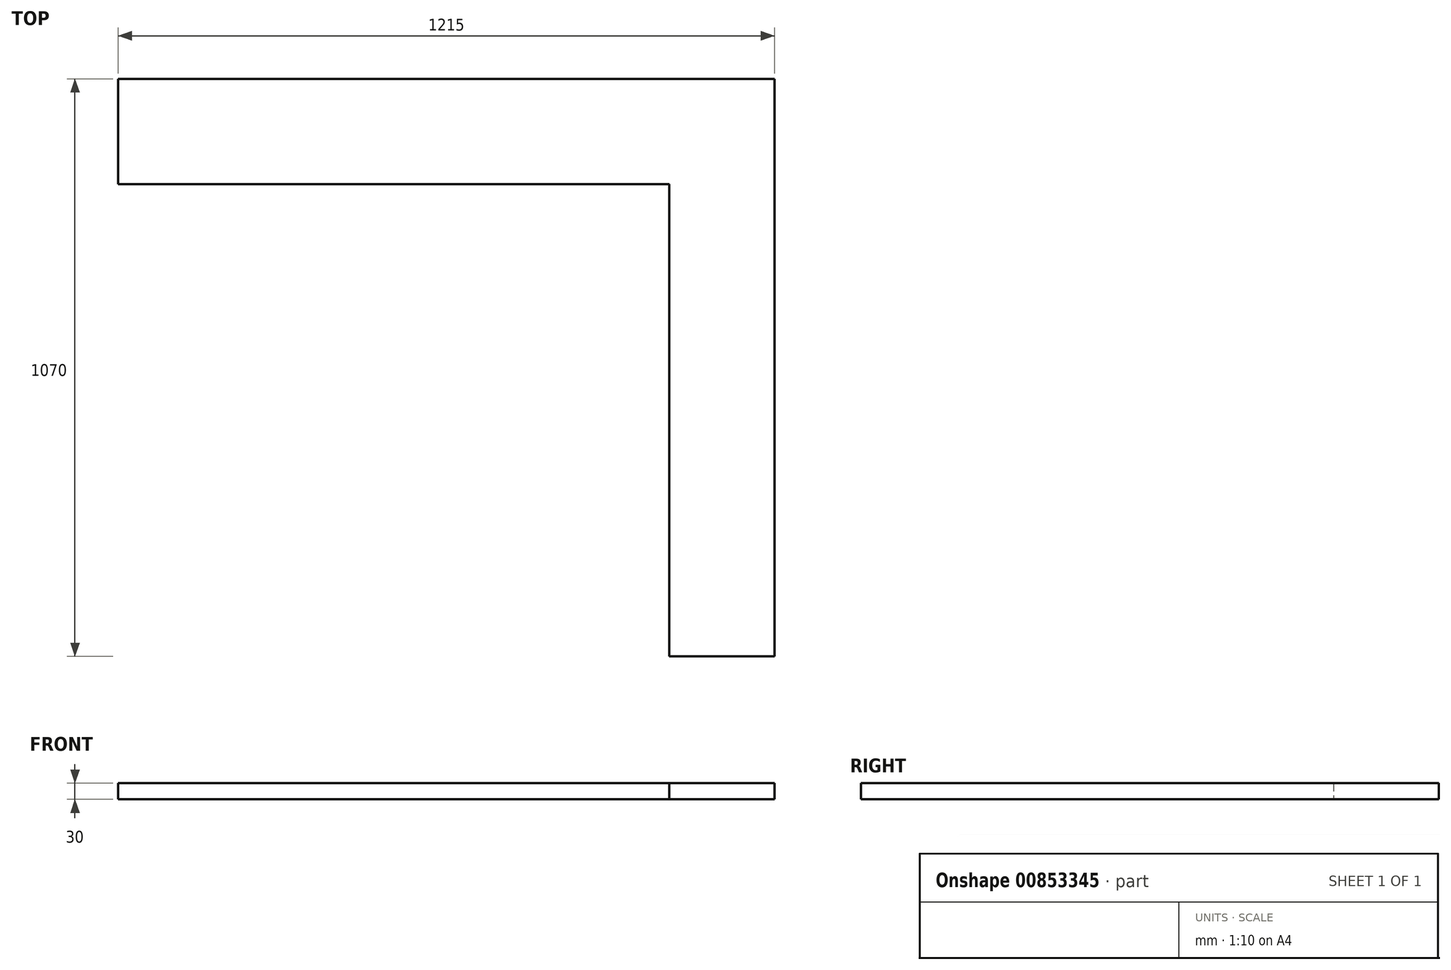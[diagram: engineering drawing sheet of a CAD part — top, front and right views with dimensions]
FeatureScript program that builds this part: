
annotation { "Feature Type Name" : "Feature", "Feature Type Description" : "" }
export const myFeature = defineFeature(function(context is Context, id is Id, definition is map)
    precondition{}
    {
        {
            var Q0;
            Q0=qCreatedBy(makeId("Top.planeOp"),FACE);
            var sketch = newSketch(context, id + "F0", { "sketchPlane" : qUnion([Q0])});
            skLineSegment(sketch, "E0", {"start": v(-114.06, 103.18) * mm, "end": v(-114.06, -91.82) * mm});
            skLineSegment(sketch, "E1", {"start": v(-114.06, 103.18) * mm, "end": v(1100.94, 103.18) * mm});
            skLineSegment(sketch, "E2", {"start": v(1100.94, 103.18) * mm, "end": v(1100.94, -966.82) * mm});
            skLineSegment(sketch, "E3", {"start": v(1100.94, -966.82) * mm, "end": v(905.94, -966.82) * mm});
            skLineSegment(sketch, "E4", {"start": v(905.94, -966.82) * mm, "end": v(905.94, -91.82) * mm});
            skLineSegment(sketch, "E5", {"start": v(-114.06, -91.82) * mm, "end": v(905.94, -91.82) * mm});
            skSolve(sketch);
        }
        {
            var Q0;
            Q0 = qSketchRegion(id + "F0", true);
            extrude(context, id + "F1", {"entities" : qUnion([Q0]), "depth" : 30 * mm, "offsetDistance" : 25 * mm});
        }
    });
